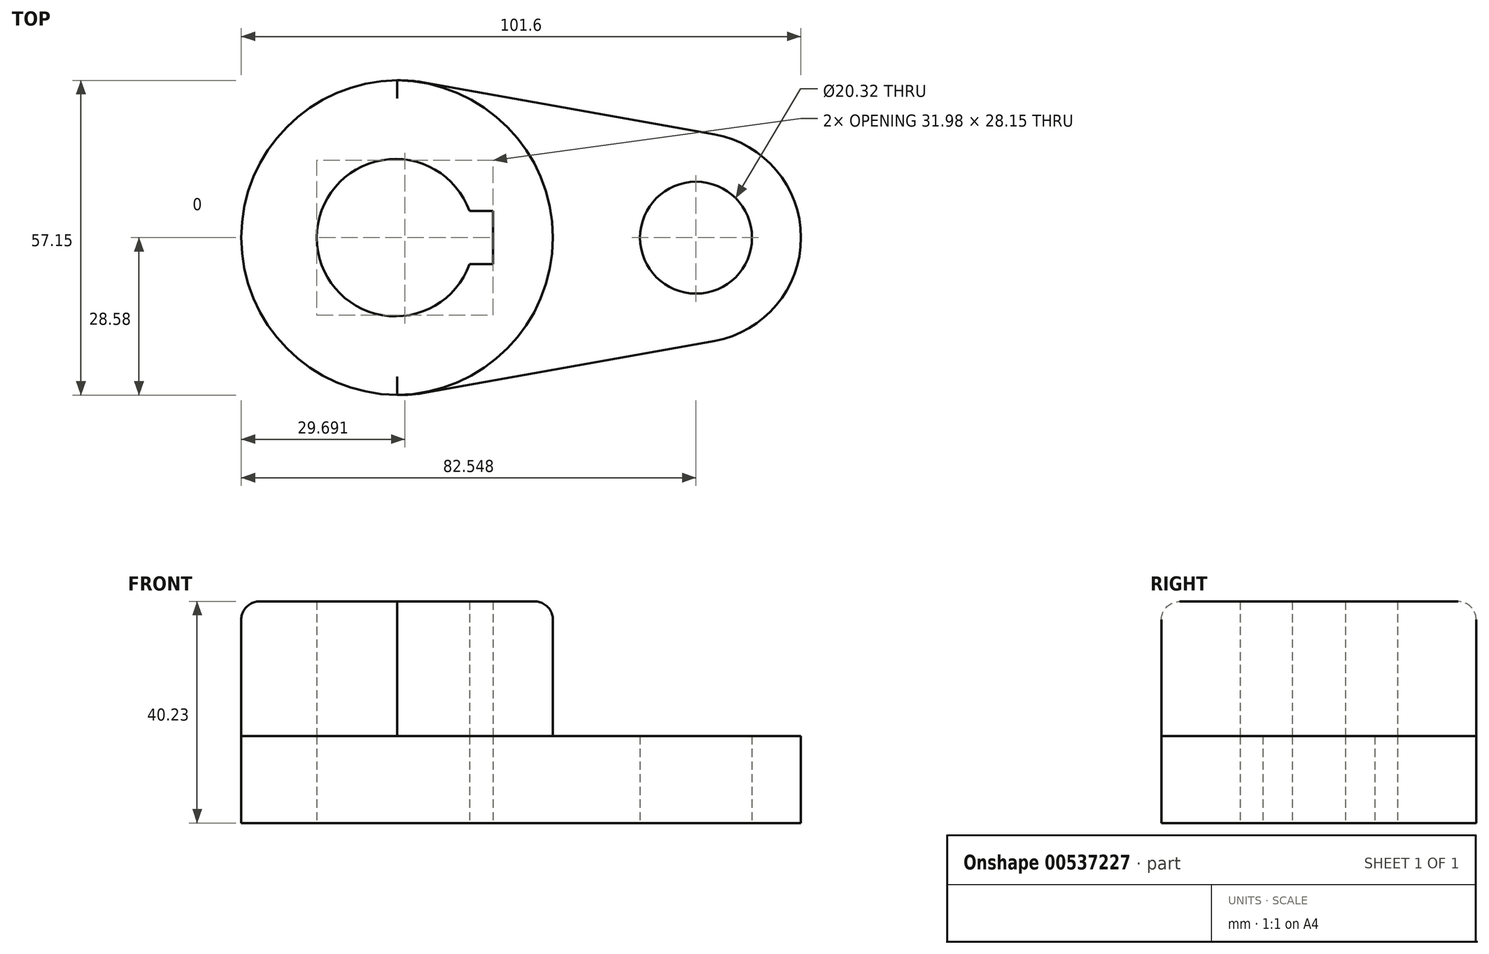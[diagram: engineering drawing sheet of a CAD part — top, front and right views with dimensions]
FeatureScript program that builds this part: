
annotation { "Feature Type Name" : "Feature", "Feature Type Description" : "" }
export const myFeature = defineFeature(function(context is Context, id is Id, definition is map)
    precondition{}
    {
        {
            var Q0;
            Q0=qCreatedBy(makeId("Top.planeOp"),FACE);
            var sketch = newSketch(context, id + "F0", { "sketchPlane" : qUnion([Q0])});
            skCircle(sketch, "E0", {"center": v(0.58, 0) * mm, "radius": 28.58 * mm});
            skArc(sketch, "E1", {"start": v(57.92, -18.75) * mm, "mid": v(73.6, 0) * mm, "end": v(57.92, 18.75) * mm});
            skLineSegment(sketch, "E2", {"start": v(5.63, 28.13) * mm, "end": v(57.92, 18.75) * mm});
            skLineSegment(sketch, "E3", {"start": v(5.63, -28.13) * mm, "end": v(57.92, -18.75) * mm});
            skCircle(sketch, "E4", {"center": v(54.56, 0) * mm, "radius": 10.16 * mm});
            skArc(sketch, "E5", {"start": v(13.45, 4.83) * mm, "mid": v(-14.29, 0) * mm, "end": v(13.45, -4.83) * mm});
            skLineSegment(sketch, "E6", {"start": v(21.63, -22.78) * mm, "end": v(21.63, -17.95) * mm});
            skLineSegment(sketch, "E7", {"start": v(17.69, 4.83) * mm, "end": v(13.45, 4.83) * mm});
            skLineSegment(sketch, "E8", {"start": v(17.69, -4.83) * mm, "end": v(13.45, -4.83) * mm});
            skLineSegment(sketch, "E9", {"start": v(17.69, 4.83) * mm, "end": v(17.69, -4.83) * mm});
            skSolve(sketch);
        }
        {
            var Q0;
            Q0=makeQuery(id+"F0.imprint","IMPRINT",FACE,{"disambiguationData":[TD([[makeQuery(id+"F0.imprint","IMPRINT",EDGE,{"derivedFrom":sQuery(id+"F0.wireOp",EDGE,"E1")}),1.0]])]});
            var Q1;
            Q1=makeQuery(id+"F0.imprint","IMPRINT",FACE,{"disambiguationData":[TD([[makeQuery(id+"F0.imprint","IMPRINT",EDGE,{"derivedFrom":sQuery(id+"F0.wireOp",EDGE,"E5")}),-1.0]])]});
            extrude(context, id + "F1", {"entities" : qUnion([Q0, Q1]), "depth" : 15.77 * mm, "offsetDistance" : 25.4 * mm});
        }
        {
            var Q0;
            Q0=makeQuery(id+"F1.opExtrude","CAP_FACE",FACE,{"disambiguationData":[OSD([sQuery(id+"F0.wireOp",EDGE,"E0"),sQuery(id+"F0.wireOp",EDGE,"E1"),sQuery(id+"F0.wireOp",EDGE,"E2"),sQuery(id+"F0.wireOp",EDGE,"E3"),sQuery(id+"F0.wireOp",EDGE,"E4"),sQuery(id+"F0.wireOp",EDGE,"E5"),sQuery(id+"F0.wireOp",EDGE,"E7"),sQuery(id+"F0.wireOp",EDGE,"E8"),sQuery(id+"F0.wireOp",EDGE,"E9")])],"isStart":false});
            var sketch = newSketch(context, id + "F2", { "sketchPlane" : qUnion([Q0])});
            skCircle(sketch, "E10", {"center": v(0, 0) * mm, "radius": 28.58 * mm});
            skSolve(sketch);
        }
        {
            var Q0;
            Q0=makeQuery(id+"F2.imprint","IMPRINT",FACE,{"disambiguationData":[TD([[makeQuery(id+"F2.imprint","IMPRINT",EDGE,{"derivedFrom":makeQuery(id+"F1.opExtrude","CAP_EDGE",EDGE,{"disambiguationData":[OSD([sQuery(id+"F0.wireOp",EDGE,"E5")])],"isStart":false})}),-1.0]])]});
            extrude(context, id + "F3", {"entities" : qUnion([Q0]), "depth" : 24.46 * mm, "offsetDistance" : 25.4 * mm});
        }
        {
            var Q0;
            Q0=makeQuery(id+"F3.opExtrude","CAP_EDGE",EDGE,{"disambiguationData":[OSD([sQuery(id+"F0.wireOp",EDGE,"E0")])],"isStart":false});
            var Q1;
            Q1=makeQuery(id+"F3.opExtrude","CAP_EDGE",EDGE,{"disambiguationData":[OSD([sQuery(id+"F2.wireOp",EDGE,"E10")])],"isStart":false});
            fillet(context, id + "F4", {"entities" : qUnion([Q0, Q1]), "radius" : 3.3 * mm, "tangentPropagation" : true, "allowEdgeOverflow" : false});
        }
    });
